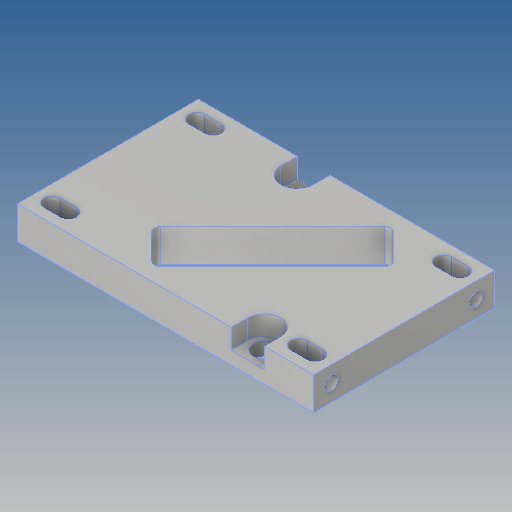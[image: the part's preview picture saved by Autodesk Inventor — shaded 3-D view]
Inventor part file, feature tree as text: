
AUTODESK INVENTOR PART (.ipt)
format: ipt  version: 2018 (Build 220112000, 112)  size: 230,400 bytes
history: native  units: mm
features: reference x18, extrude x7, sketch x7, other x3, projected_geometry x1
ambient origin geometry x8: Origin, YZ Plane, XZ Plane, XY Plane, X Axis, Y Axis, Z Axis, Center Point
bodies: Solid1 (feature_tree)
feature tree (36):
  extrude  "Extrusion1"  Depth=90.0mm
  extrude  "Extrusion2"  Depth=10.0mm
  extrude  "Extrusion3"  Depth=20.0mm
  extrude  "Extrusion4"  Depth=55.0mm
  extrude  "Extrusion5"  Depth=6.6mm
  extrude  "Extrusion6"  Depth=10.0mm
  extrude  "Extrusion7"  Depth=6.0mm TaperAngle=0.0deg
  sketch  "Sketch1"  dims[d0=55.0mm d1=90.0mm]
  sketch  "Sketch3"  dims[d2=10.0mm d3=0.0mm d4=5.0mm]
  reference  "Reference1"
  sketch  "Sketch4"  dims[d5=5.0mm d6=20.0mm]
  sketch  "Sketch5"  dims[d7=82.207357mm d8=55.0mm]
  reference  "Reference2"
  reference  "Reference3"
  reference  "Reference4"
  reference  "Reference5"
  reference  "Reference6"
  reference  "Reference7"
  projected_geometry  "Projected Loop1"
  reference  "Reference8"
  reference  "Reference9"
  reference  "Reference10"
  sketch  "Sketch6"  dims[d9=6.6mm d10=6.6mm]
  sketch  "Sketch7"  dims[d11=10.0mm d12=0.0mm d13=10.0mm]
  sketch  "Sketch8"  dims[d14=6.0mm d15=0.0mm d16=6.0mm d17=0.0mm d18=5.0mm d19=5.0mm d20=3.0mm d21=5.0mm d22=5.0mm d23=6.0mm d24=0.0mm d25=5.5mm d26=4.0mm d27=5.0mm d28=4.0mm d29=5.5mm d30=5.0mm d31=14.0mm d32=0.0mm d33=14.0mm d34=0.0mm]
  reference  "Reference11"
  reference  "Reference12"
  reference  "Reference13"
  reference  "Reference14"
  reference  "Reference15"
  reference  "Reference16"
  reference  "Reference17"
  reference  "Reference18"
  other  "<userpath>\OneDrive\Objet3D\EPFLEplucheCarrote\V7\AssemblyPeleCarotte-SURFACE-NAT.iam"
  other  "AssemblyPeleCarotte-SURFACE-NAT.iam"
  other  "GuideCarotte:1"
